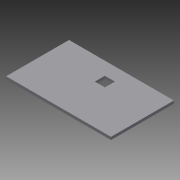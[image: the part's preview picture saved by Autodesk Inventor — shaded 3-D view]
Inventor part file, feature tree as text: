
AUTODESK INVENTOR PART (.ipt)
format: ipt  version: 2013 SP2 (Build 170200200, 200)  size: 218,112 bytes
history: native  units: in
note: dims shown in document units (in); Inventor stores cm internally (conversion verified against a paired STEP export)
features: extrude x3, sketch x2
ambient origin geometry x8: Origin, YZ Plane, XZ Plane, XY Plane, X Axis, Y Axis, Z Axis, Center Point
bodies: Solid1 (feature_tree)
feature tree (5):
  extrude  "Extrusion1"  Depth=46.0in
  sketch  "Sketch2"  dims[d17=46.0in d18=60.0in d19=224.0in d20=12.0in d21=0.0in d22=288.0in d23=24.0in d24=40.875in d25=36.0in d26=4.5in d27=40.875in d28=40.875in d29=36.0in d30=48.0in d31=24.0in d32=168.0in d33=72.0in d34=480.0in d35=24.0in d36=4.5in d40=0.05in d41=0.05in d42=0.06in d43=0.5in d44=0.05in d45=48.0in d46=0.75in d47=0.0in d48=0.05in d49=0.75in d50=0.0in d51=0.05in]
  extrude  "Extrusion3"  Depth=60.0in
  extrude  "Extrusion4"  Depth=224.0in
  sketch  "Sketch1"  dims[d0=288.0in d12=480.0in d16=46.0in]
